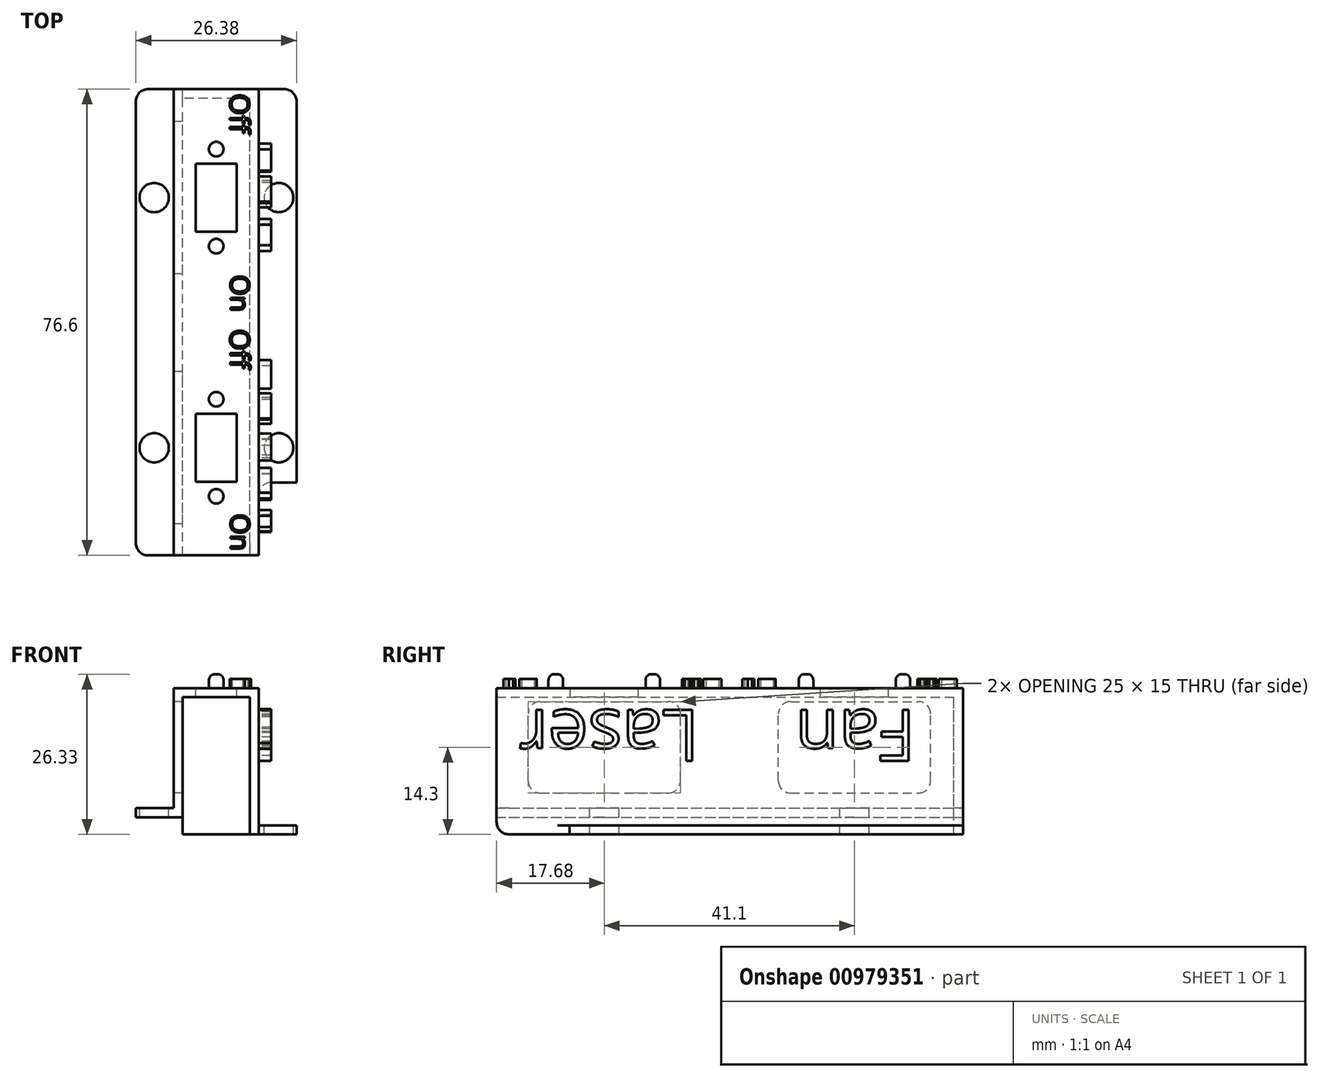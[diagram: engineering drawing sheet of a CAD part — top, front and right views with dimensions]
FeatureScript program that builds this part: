
annotation { "Feature Type Name" : "Feature", "Feature Type Description" : "" }
export const myFeature = defineFeature(function(context is Context, id is Id, definition is map)
    precondition{}
    {
        {
            var Q0;
            Q0=qCreatedBy(makeId("Front.planeOp"),FACE);
            var sketch = newSketch(context, id + "F0", { "sketchPlane" : qUnion([Q0])});
            skLineSegment(sketch, "E0", {"start": v(0, 0) * mm, "end": v(0, 1.5) * mm});
            skLineSegment(sketch, "E1", {"start": v(0, 1.5) * mm, "end": v(6.19, 1.5) * mm});
            skLineSegment(sketch, "E2", {"start": v(6.19, 1.5) * mm, "end": v(6.19, 21.23) * mm});
            skLineSegment(sketch, "E3", {"start": v(6.19, 21.23) * mm, "end": v(20.2, 21.23) * mm});
            skLineSegment(sketch, "E4", {"start": v(20.2, 21.23) * mm, "end": v(20.2, -1.3) * mm});
            skLineSegment(sketch, "E5", {"start": v(20.2, -1.3) * mm, "end": v(26.38, -1.3) * mm});
            skLineSegment(sketch, "E6", {"start": v(26.38, -1.3) * mm, "end": v(26.38, -2.8) * mm});
            skLineSegment(sketch, "E7", {"start": v(26.38, -2.8) * mm, "end": v(18.7, -2.8) * mm});
            skLineSegment(sketch, "E8", {"start": v(18.7, -2.8) * mm, "end": v(18.7, 19.73) * mm});
            skLineSegment(sketch, "E9", {"start": v(18.7, 19.73) * mm, "end": v(7.69, 19.73) * mm});
            skLineSegment(sketch, "E10", {"start": v(7.69, 19.73) * mm, "end": v(7.69, 0) * mm});
            skLineSegment(sketch, "E11", {"start": v(7.7, 0) * mm, "end": v(0, 0) * mm});
            skSolve(sketch);
        }
        {
            var Q0;
            Q0=makeQuery(id+"F0.imprint","IMPRINT",FACE,{"disambiguationData":[TD([[makeQuery(id+"F0.imprint","IMPRINT",EDGE,{"derivedFrom":sQuery(id+"F0.wireOp",EDGE,"E0")}),-1.0]])]});
            extrude(context, id + "F1", {"entities" : qUnion([Q0]), "depth" : 76.6 * mm, "offsetDistance" : 25 * mm});
        }
        {
            var Q0;
            Q0=makeQuery(id+"F1.opExtrude","SWEPT_FACE",FACE,{"disambiguationData":[OSD([sQuery(id+"F0.wireOp",EDGE,"E1")])]});
            var sketch = newSketch(context, id + "F2", { "sketchPlane" : qUnion([Q0])});
            skCircle(sketch, "E12", {"center": v(3, -17.82) * mm, "radius": 2.4 * mm});
            skCircle(sketch, "E13", {"center": v(3, -58.92) * mm, "radius": 2.4 * mm});
            skCircle(sketch, "E14", {"center": v(23.47, -17.82) * mm, "radius": 2.4 * mm});
            skCircle(sketch, "E15", {"center": v(23.47, -58.92) * mm, "radius": 2.4 * mm});
            skSolve(sketch);
        }
        {
            var Q0;
            Q0=makeQuery(id+"F2.imprint","IMPRINT",FACE,{"disambiguationData":[TD([[makeQuery(id+"F2.imprint","IMPRINT",EDGE,{"derivedFrom":sQuery(id+"F2.wireOp",EDGE,"E12")}),1.0]])]});
            var Q1;
            Q1=makeQuery(id+"F2.imprint","IMPRINT",FACE,{"disambiguationData":[TD([[makeQuery(id+"F2.imprint","IMPRINT",EDGE,{"derivedFrom":sQuery(id+"F2.wireOp",EDGE,"E13")}),1.0]])]});
            var Q2;
            Q2=makeQuery(id+"F2.imprint","IMPRINT",FACE,{"disambiguationData":[TD([[makeQuery(id+"F2.imprint","IMPRINT",EDGE,{"derivedFrom":sQuery(id+"F2.wireOp",EDGE,"E15")}),1.0]])]});
            var Q3;
            Q3=makeQuery(id+"F2.imprint","IMPRINT",FACE,{"disambiguationData":[TD([[makeQuery(id+"F2.imprint","IMPRINT",EDGE,{"derivedFrom":sQuery(id+"F2.wireOp",EDGE,"E14")}),1.0]])]});
            extrude(context, id + "F3", {"entities" : qUnion([Q0, Q1, Q2, Q3]), "operationType" : NewBodyOperationType.REMOVE, "oppositeDirection" : true, "depth" : 10 * mm, "offsetDistance" : 25 * mm});
        }
        {
            var Q0;
            Q0=makeQuery(id+"F1.opExtrude","SWEPT_FACE",FACE,{"disambiguationData":[OSD([sQuery(id+"F0.wireOp",EDGE,"E2")])]});
            var sketch = newSketch(context, id + "F4", { "sketchPlane" : qUnion([Q0])});
            skLineSegment(sketch, "E16.bottom", {"start": v(30.32, 4) * mm, "end": v(5.32, 4) * mm});
            skLineSegment(sketch, "E16.top", {"start": v(30.32, 19) * mm, "end": v(5.32, 19) * mm});
            skLineSegment(sketch, "E16.left", {"start": v(30.32, 4) * mm, "end": v(30.32, 19) * mm});
            skLineSegment(sketch, "E16.right", {"start": v(5.32, 4) * mm, "end": v(5.32, 19) * mm});
            skPoint(sketch, "E16.middle", {"position": v(17.82, 11.5) * mm});
            skLineSegment(sketch, "E17.bottom", {"start": v(71.42, 4) * mm, "end": v(46.42, 4) * mm});
            skLineSegment(sketch, "E17.top", {"start": v(71.42, 19) * mm, "end": v(46.42, 19) * mm});
            skLineSegment(sketch, "E17.left", {"start": v(71.42, 4) * mm, "end": v(71.42, 19) * mm});
            skLineSegment(sketch, "E17.right", {"start": v(46.42, 4) * mm, "end": v(46.42, 19) * mm});
            skPoint(sketch, "E17.middle", {"position": v(58.92, 11.5) * mm});
            skSolve(sketch);
        }
        {
            var Q0;
            Q0=makeQuery(id+"F4.imprint","IMPRINT",FACE,{"disambiguationData":[TD([[makeQuery(id+"F4.imprint","IMPRINT",EDGE,{"derivedFrom":sQuery(id+"F4.wireOp",EDGE,"E16.bottom")}),-1.0]])]});
            var Q1;
            Q1=makeQuery(id+"F4.imprint","IMPRINT",FACE,{"disambiguationData":[TD([[makeQuery(id+"F4.imprint","IMPRINT",EDGE,{"derivedFrom":sQuery(id+"F4.wireOp",EDGE,"E17.bottom")}),-1.0]])]});
            extrude(context, id + "F5", {"entities" : qUnion([Q0, Q1]), "operationType" : NewBodyOperationType.REMOVE, "endBound" : BoundingType.UP_TO_NEXT, "oppositeDirection" : true, "depth" : 25 * mm, "offsetDistance" : 25 * mm});
        }
        {
            var Q0;
            Q0=makeQuery(id+"F1.opExtrude","SWEPT_FACE",FACE,{"disambiguationData":[OSD([sQuery(id+"F0.wireOp",EDGE,"E3")])]});
            var sketch = newSketch(context, id + "F6", { "sketchPlane" : qUnion([Q0])});
            skLineSegment(sketch, "E18", {"start": v(13.2, 0) * mm, "end": v(13.2, -86.72) * mm, "construction": true});
            skLineSegment(sketch, "E19.bottom", {"start": v(16.54, -12.22) * mm, "end": v(9.84, -12.22) * mm});
            skLineSegment(sketch, "E19.top", {"start": v(16.54, -23.42) * mm, "end": v(9.84, -23.42) * mm});
            skLineSegment(sketch, "E19.left", {"start": v(16.54, -12.22) * mm, "end": v(16.54, -23.42) * mm});
            skLineSegment(sketch, "E19.right", {"start": v(9.84, -12.22) * mm, "end": v(9.84, -23.42) * mm});
            skPoint(sketch, "E19.middle", {"position": v(13.2, -17.82) * mm});
            skLineSegment(sketch, "E20.bottom", {"start": v(16.54, -53.32) * mm, "end": v(9.84, -53.32) * mm});
            skLineSegment(sketch, "E20.top", {"start": v(16.54, -64.52) * mm, "end": v(9.84, -64.52) * mm});
            skLineSegment(sketch, "E20.left", {"start": v(16.54, -53.32) * mm, "end": v(16.54, -64.52) * mm});
            skLineSegment(sketch, "E20.right", {"start": v(9.84, -53.32) * mm, "end": v(9.84, -64.52) * mm});
            skPoint(sketch, "E20.middle", {"position": v(13.2, -58.92) * mm});
            skSolve(sketch);
        }
        {
            var Q0;
            Q0=makeQuery(id+"F6.imprint","IMPRINT",FACE,{"disambiguationData":[TD([[makeQuery(id+"F6.imprint","IMPRINT",EDGE,{"derivedFrom":sQuery(id+"F6.wireOp",EDGE,"E19.bottom")}),1.0]])]});
            var Q1;
            Q1=makeQuery(id+"F6.imprint","IMPRINT",FACE,{"disambiguationData":[TD([[makeQuery(id+"F6.imprint","IMPRINT",EDGE,{"derivedFrom":sQuery(id+"F6.wireOp",EDGE,"E20.bottom")}),1.0]])]});
            extrude(context, id + "F7", {"entities" : qUnion([Q0, Q1]), "operationType" : NewBodyOperationType.REMOVE, "endBound" : BoundingType.UP_TO_NEXT, "oppositeDirection" : true, "depth" : 25 * mm, "offsetDistance" : 25 * mm});
        }
        {
            var Q0;
            Q0=makeQuery(id+"F1.opExtrude","SWEPT_FACE",FACE,{"disambiguationData":[OSD([sQuery(id+"F0.wireOp",EDGE,"E3")])]});
            var sketch = newSketch(context, id + "F8", { "sketchPlane" : qUnion([Q0])});
            skCircle(sketch, "E21", {"center": v(13.19, -66.89) * mm, "radius": 1.2 * mm});
            skPoint(sketch, "E21.centerSnap0", {"position": v(13.19, -64.52) * mm});
            skCircle(sketch, "E22", {"center": v(13.19, -50.95) * mm, "radius": 1.2 * mm});
            skPoint(sketch, "E22.centerSnap0", {"position": v(13.19, -53.32) * mm});
            skCircle(sketch, "E23", {"center": v(13.19, -25.8) * mm, "radius": 1.2 * mm});
            skPoint(sketch, "E23.centerSnap0", {"position": v(13.19, -23.42) * mm});
            skCircle(sketch, "E24", {"center": v(13.19, -9.85) * mm, "radius": 1.2 * mm});
            skPoint(sketch, "E24.centerSnap0", {"position": v(13.19, -12.22) * mm});
            skSolve(sketch);
        }
        {
            var Q0;
            Q0=makeQuery(id+"F8.imprint","IMPRINT",FACE,{"disambiguationData":[TD([[makeQuery(id+"F8.imprint","IMPRINT",EDGE,{"derivedFrom":sQuery(id+"F8.wireOp",EDGE,"E24")}),1.0]])]});
            var Q1;
            Q1=makeQuery(id+"F8.imprint","IMPRINT",FACE,{"disambiguationData":[TD([[makeQuery(id+"F8.imprint","IMPRINT",EDGE,{"derivedFrom":sQuery(id+"F8.wireOp",EDGE,"E23")}),1.0]])]});
            var Q2;
            Q2=makeQuery(id+"F8.imprint","IMPRINT",FACE,{"disambiguationData":[TD([[makeQuery(id+"F8.imprint","IMPRINT",EDGE,{"derivedFrom":sQuery(id+"F8.wireOp",EDGE,"E22")}),1.0]])]});
            var Q3;
            Q3=makeQuery(id+"F8.imprint","IMPRINT",FACE,{"disambiguationData":[TD([[makeQuery(id+"F8.imprint","IMPRINT",EDGE,{"derivedFrom":sQuery(id+"F8.wireOp",EDGE,"E21")}),1.0]])]});
            extrude(context, id + "F9", {"entities" : qUnion([Q0, Q1, Q2, Q3]), "operationType" : NewBodyOperationType.ADD, "depth" : 2.3 * mm, "offsetDistance" : 25 * mm});
        }
        {
            var Q0;
            Q0=makeQuery(id+"F9.opExtrude","CAP_EDGE",EDGE,{"disambiguationData":[OSD([sQuery(id+"F8.wireOp",EDGE,"E24")])],"isStart":false});
            var Q1;
            Q1=makeQuery(id+"F9.opExtrude","CAP_EDGE",EDGE,{"disambiguationData":[OSD([sQuery(id+"F8.wireOp",EDGE,"E23")])],"isStart":false});
            var Q2;
            Q2=makeQuery(id+"F9.opExtrude","CAP_EDGE",EDGE,{"disambiguationData":[OSD([sQuery(id+"F8.wireOp",EDGE,"E22")])],"isStart":false});
            var Q3;
            Q3=makeQuery(id+"F9.opExtrude","CAP_EDGE",EDGE,{"disambiguationData":[OSD([sQuery(id+"F8.wireOp",EDGE,"E21")])],"isStart":false});
            fillet(context, id + "F10", {"entities" : qUnion([Q0, Q1, Q2, Q3]), "radius" : 1 * mm, "tangentPropagation" : true, "allowEdgeOverflow" : false});
        }
        {
            var Q0;
            Q0=makeQuery(id+"F5.boolean.opBoolean","COPY",EDGE,{"derivedFrom":makeQuery(id+"F5.opExtrude","SWEPT_EDGE",EDGE,{"disambiguationData":[OSD([sQuery(id+"F4.wireOp",EDGE,"E16.bottom"),sQuery(id+"F4.wireOp",EDGE,"E16.right")])]})});
            var Q1;
            Q1=makeQuery(id+"F5.boolean.opBoolean","COPY",EDGE,{"derivedFrom":makeQuery(id+"F5.opExtrude","SWEPT_EDGE",EDGE,{"disambiguationData":[OSD([sQuery(id+"F4.wireOp",EDGE,"E16.top"),sQuery(id+"F4.wireOp",EDGE,"E16.right")])]})});
            var Q2;
            Q2=makeQuery(id+"F5.boolean.opBoolean","COPY",EDGE,{"derivedFrom":makeQuery(id+"F5.opExtrude","SWEPT_EDGE",EDGE,{"disambiguationData":[OSD([sQuery(id+"F4.wireOp",EDGE,"E16.top"),sQuery(id+"F4.wireOp",EDGE,"E16.left")])]})});
            var Q3;
            Q3=makeQuery(id+"F5.boolean.opBoolean","COPY",EDGE,{"derivedFrom":makeQuery(id+"F5.opExtrude","SWEPT_EDGE",EDGE,{"disambiguationData":[OSD([sQuery(id+"F4.wireOp",EDGE,"E16.bottom"),sQuery(id+"F4.wireOp",EDGE,"E16.left")])]})});
            var Q4;
            Q4=makeQuery(id+"F5.boolean.opBoolean","COPY",EDGE,{"derivedFrom":makeQuery(id+"F5.opExtrude","SWEPT_EDGE",EDGE,{"disambiguationData":[OSD([sQuery(id+"F4.wireOp",EDGE,"E17.top"),sQuery(id+"F4.wireOp",EDGE,"E17.right")])]})});
            var Q5;
            Q5=makeQuery(id+"F5.boolean.opBoolean","COPY",EDGE,{"derivedFrom":makeQuery(id+"F5.opExtrude","SWEPT_EDGE",EDGE,{"disambiguationData":[OSD([sQuery(id+"F4.wireOp",EDGE,"E17.bottom"),sQuery(id+"F4.wireOp",EDGE,"E17.right")])]})});
            var Q6;
            Q6=makeQuery(id+"F5.boolean.opBoolean","COPY",EDGE,{"derivedFrom":makeQuery(id+"F5.opExtrude","SWEPT_EDGE",EDGE,{"disambiguationData":[OSD([sQuery(id+"F4.wireOp",EDGE,"E17.top"),sQuery(id+"F4.wireOp",EDGE,"E17.left")])]})});
            var Q7;
            Q7=makeQuery(id+"F5.boolean.opBoolean","COPY",EDGE,{"derivedFrom":makeQuery(id+"F5.opExtrude","SWEPT_EDGE",EDGE,{"disambiguationData":[OSD([sQuery(id+"F4.wireOp",EDGE,"E17.bottom"),sQuery(id+"F4.wireOp",EDGE,"E17.left")])]})});
            fillet(context, id + "F11", {"entities" : qUnion([Q0, Q1, Q2, Q3, Q4, Q5, Q6, Q7]), "radius" : 2 * mm, "tangentPropagation" : true, "allowEdgeOverflow" : false});
        }
        {
            var Q0;
            Q0=makeQuery(id+"F1.opExtrude","SWEPT_FACE",FACE,{"disambiguationData":[OSD([sQuery(id+"F0.wireOp",EDGE,"E3")])]});
            var sketch = newSketch(context, id + "F12", { "sketchPlane" : qUnion([Q0])});
            skText(sketch, "E25", { "text": "Off", "fontName": "OpenSans-Regular.ttf"});
            skText(sketch, "E26", { "text": "On", "fontName": "OpenSans-Regular.ttf"});
            skText(sketch, "E27", { "text": "Off", "fontName": "OpenSans-Regular.ttf"});
            skText(sketch, "E28", { "text": "On", "fontName": "OpenSans-Regular.ttf"});
            const initialGuessF12  = {"E25": [0.01546, -0.03942, 0, -1, 0.00322], "E26": [0.01554, -0.06975, 0, -1, 0.00314], "E27": [0.01544, -0.00075, 0, -1, 0.00322], "E28": [0.01552, -0.0305, 0, -1, 0.00314]};
            skSetInitialGuess(sketch, initialGuessF12);
            skSolve(sketch);
        }
        {
            var Q0;
            Q0=qSketchRegion(id+"F12",true);
            extrude(context, id + "F13", {"entities" : qUnion([Q0]), "operationType" : NewBodyOperationType.ADD, "depth" : 1.5 * mm, "offsetDistance" : 25 * mm});
        }
        {
            var Q0;
            Q0=makeQuery(id+"F1.opExtrude","SWEPT_FACE",FACE,{"disambiguationData":[OSD([sQuery(id+"F0.wireOp",EDGE,"E5")])]});
            var sketch = newSketch(context, id + "F14", { "sketchPlane" : qUnion([Q0])});
            skLineSegment(sketch, "E29.bottom", {"start": v(26.38, -64.62) * mm, "end": v(20.2, -64.62) * mm});
            skLineSegment(sketch, "E29.top", {"start": v(26.38, -76.6) * mm, "end": v(20.2, -76.6) * mm});
            skLineSegment(sketch, "E29.left", {"start": v(26.38, -64.62) * mm, "end": v(26.38, -76.6) * mm});
            skLineSegment(sketch, "E29.right", {"start": v(20.2, -64.62) * mm, "end": v(20.2, -76.6) * mm});
            skSolve(sketch);
        }
        {
            var Q0;
            {var subQ4=sQuery(id+"F14.wireOp",EDGE,"E29.bottom");Q0=makeQuery(id+"F14.imprint","IMPRINT",FACE,{"disambiguationData":[TD([[makeQuery(id+"F14.imprint","IMPRINT",EDGE,{"derivedFrom":subQ4}),1.0]])]});}
            extrude(context, id + "F15", {"entities" : qUnion([Q0]), "operationType" : NewBodyOperationType.REMOVE, "endBound" : BoundingType.UP_TO_NEXT, "oppositeDirection" : true, "depth" : 25 * mm, "offsetDistance" : 25 * mm});
        }
        {
            var Q0;
            Q0=makeQuery(id+"F15.boolean.opBoolean","MERGE",FACE,{"derivedFrom":[makeQuery(id+"F1.opExtrude","SWEPT_FACE",FACE,{"disambiguationData":[OSD([sQuery(id+"F0.wireOp",EDGE,"E4")])]})],"fromTools":[makeQuery(id+"F15.opExtrude","SWEPT_FACE",FACE,{"disambiguationData":[OSD([sQuery(id+"F14.wireOp",EDGE,"E29.right")])]})]});
            var sketch = newSketch(context, id + "F16", { "sketchPlane" : qUnion([Q0])});
            skPoint(sketch, "E30", {"position": v(-30.9, -0.48) * mm});
            skText(sketch, "E31", { "text": "Fan", "fontName": "OpenSans-Regular.ttf"});
            skText(sketch, "E32", { "text": "Laser", "fontName": "OpenSans-Regular.ttf"});
            const initialGuessF16  = {"E31": [-0.00778, 0.01765, -1, 0, 0.00844], "E32": [-0.04336, 0.01765, -1, 0, 0.00844]};
            skSetInitialGuess(sketch, initialGuessF16);
            skSolve(sketch);
        }
        {
            var Q0;
            Q0 = qSketchRegion(id + "F16", true);
            extrude(context, id + "F17", {"entities" : qUnion([Q0]), "operationType" : NewBodyOperationType.ADD, "depth" : 2 * mm, "offsetDistance" : 25 * mm});
        }
        {
            var Q0;
            Q0=makeQuery(id+"F1.opExtrude","SWEPT_FACE",FACE,{"disambiguationData":[OSD([sQuery(id+"F0.wireOp",EDGE,"E9")])]});
            var sketch = newSketch(context, id + "F18", { "sketchPlane" : qUnion([Q0])});
            skLineSegment(sketch, "E33.bottom", {"start": v(18.7, 0) * mm, "end": v(7.7, 0) * mm});
            skLineSegment(sketch, "E33.top", {"start": v(18.7, 1.5) * mm, "end": v(7.7, 1.5) * mm});
            skLineSegment(sketch, "E33.left", {"start": v(18.7, 0) * mm, "end": v(18.7, 1.5) * mm});
            skLineSegment(sketch, "E33.right", {"start": v(7.7, 0) * mm, "end": v(7.7, 1.5) * mm});
            skSolve(sketch);
        }
        {
            var Q0;
            Q0=makeQuery(id+"F18.imprint","IMPRINT",FACE,{"disambiguationData":[TD([[makeQuery(id+"F18.imprint","IMPRINT",EDGE,{"derivedFrom":sQuery(id+"F18.wireOp",EDGE,"E33.bottom")}),-1.0]])]});
            extrude(context, id + "F19", {"entities" : qUnion([Q0]), "operationType" : NewBodyOperationType.ADD, "depth" : 22.53 * mm, "offsetDistance" : 25 * mm});
        }
        {
            var Q0;
            Q0=makeQuery(id+"F1.opExtrude","CAP_EDGE",EDGE,{"disambiguationData":[OSD([sQuery(id+"F0.wireOp",EDGE,"E6")])],"isStart":true});
            var Q1;
            Q1=makeQuery(id+"F1.opExtrude","CAP_EDGE",EDGE,{"disambiguationData":[OSD([sQuery(id+"F0.wireOp",EDGE,"E0")])],"isStart":true});
            var Q2;
            Q2=makeQuery(id+"F1.opExtrude","CAP_EDGE",EDGE,{"disambiguationData":[OSD([sQuery(id+"F0.wireOp",EDGE,"E6")])],"isStart":false});
            var Q3;
            Q3=makeQuery(id+"F1.opExtrude","CAP_EDGE",EDGE,{"disambiguationData":[OSD([sQuery(id+"F0.wireOp",EDGE,"E0")])],"isStart":false});
            var Q4;
            Q4=makeQuery(id+"F15.boolean.opBoolean","COPY",EDGE,{"derivedFrom":makeQuery(id+"F15.opExtrude","SWEPT_EDGE",EDGE,{"disambiguationData":[OSD([sQuery(id+"F0.wireOp",EDGE,"E5"),sQuery(id+"F0.wireOp",EDGE,"E6"),sQuery(id+"F14.wireOp",EDGE,"E29.bottom"),sQuery(id+"F14.wireOp",EDGE,"E29.left")])]})});
            var Q5;
            Q5=makeQuery(id+"F15.boolean.opBoolean","COPY",EDGE,{"derivedFrom":makeQuery(id+"F15.opExtrude","SWEPT_EDGE",EDGE,{"disambiguationData":[OSD([sQuery(id+"F0.wireOp",EDGE,"E4"),sQuery(id+"F0.wireOp",EDGE,"E5"),sQuery(id+"F14.wireOp",EDGE,"E29.bottom"),sQuery(id+"F14.wireOp",EDGE,"E29.right")])]})});
            var Q6;
            Q6=makeQuery(id+"F1.opExtrude","CAP_EDGE",EDGE,{"disambiguationData":[OSD([sQuery(id+"F0.wireOp",EDGE,"E7")])],"isStart":false});
            fillet(context, id + "F20", {"entities" : qUnion([Q0, Q1, Q2, Q3, Q4, Q5, Q6]), "radius" : 2 * mm, "tangentPropagation" : true, "allowEdgeOverflow" : false});
        }
    });
